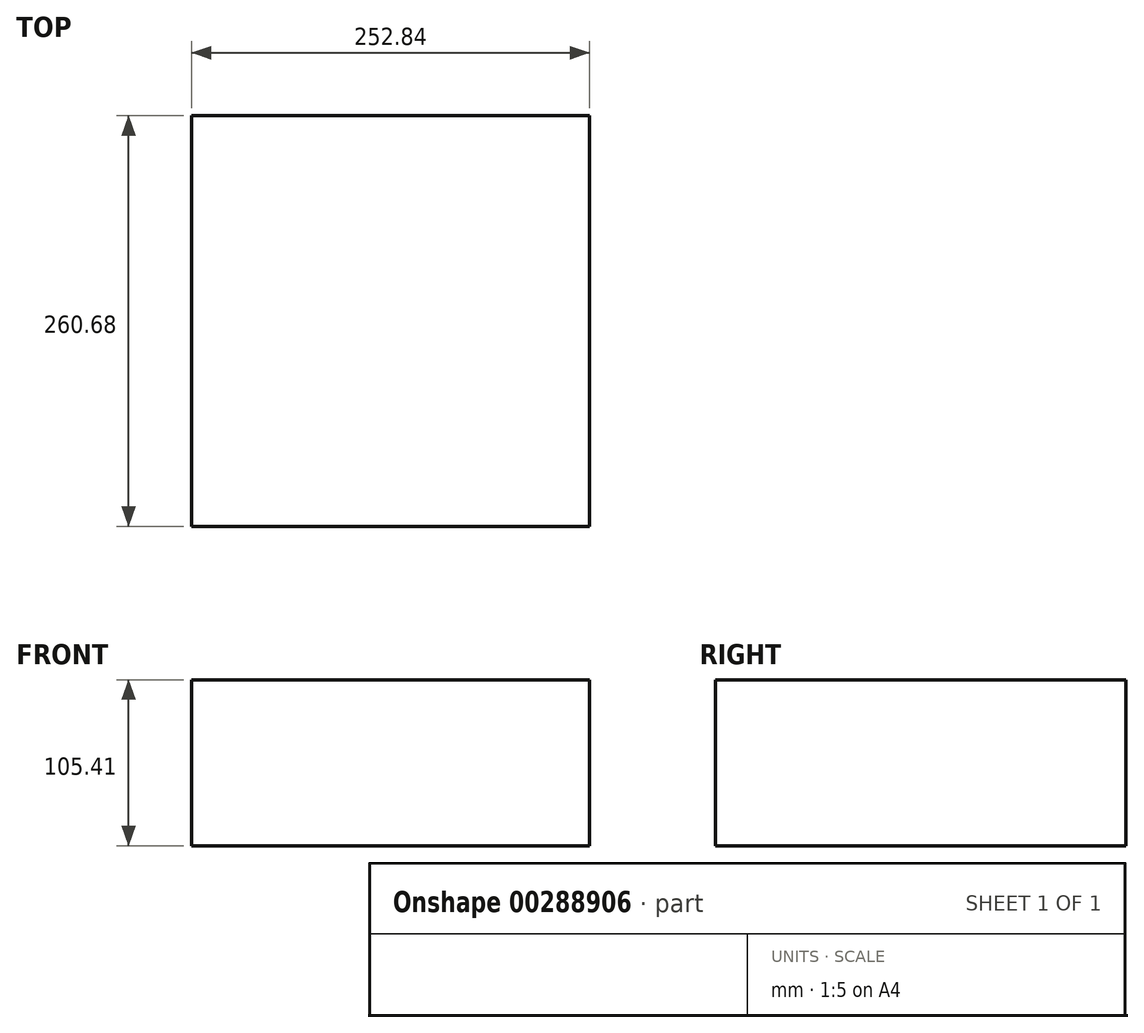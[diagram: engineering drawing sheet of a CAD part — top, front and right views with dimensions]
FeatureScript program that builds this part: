
annotation { "Feature Type Name" : "Feature", "Feature Type Description" : "" }
export const myFeature = defineFeature(function(context is Context, id is Id, definition is map)
    precondition{}
    {
        {
            var Q0;
            Q0=qCreatedBy(makeId("Top.planeOp"),FACE);
            var sketch = newSketch(context, id + "F0", { "sketchPlane" : qUnion([Q0])});
            skLineSegment(sketch, "E0.bottom", {"start": v(0, 0) * mm, "end": v(252.84, 0) * mm});
            skLineSegment(sketch, "E0.top", {"start": v(0, 260.68) * mm, "end": v(252.84, 260.68) * mm});
            skLineSegment(sketch, "E0.left", {"start": v(0, 0) * mm, "end": v(0, 260.68) * mm});
            skLineSegment(sketch, "E0.right", {"start": v(252.84, 0) * mm, "end": v(252.84, 260.68) * mm});
            skSolve(sketch);
        }
        {
            var Q0;
            Q0 = qSketchRegion(id + "F0", true);
            extrude(context, id + "F1", {"entities" : qUnion([Q0]), "depth" : 105.4 * mm});
        }
    });
